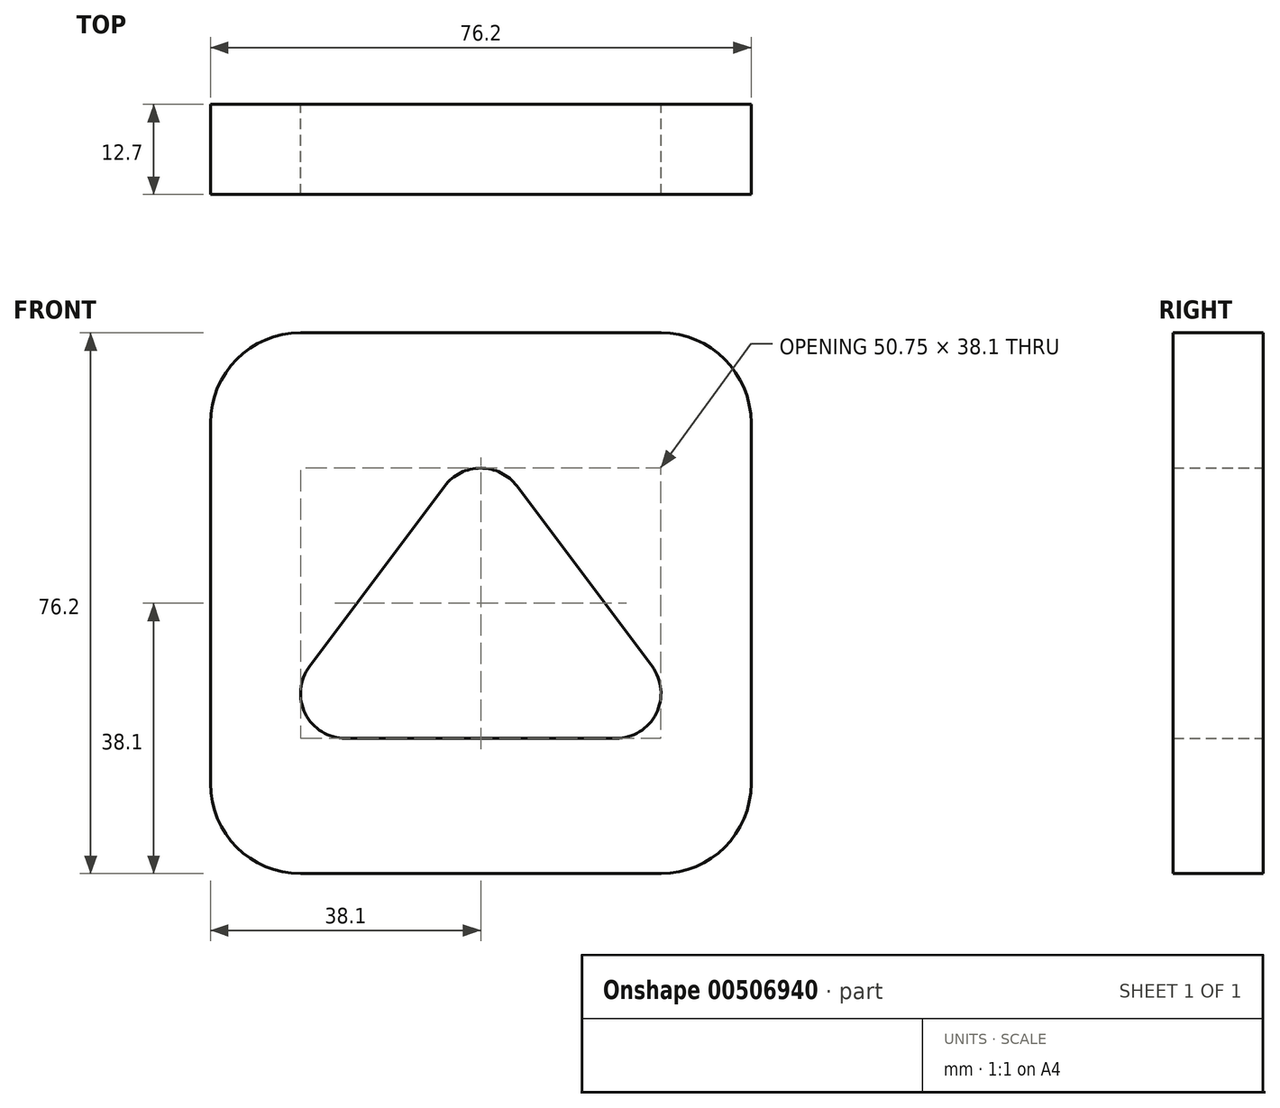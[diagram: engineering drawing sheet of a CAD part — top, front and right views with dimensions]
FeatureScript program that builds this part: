
annotation { "Feature Type Name" : "Feature", "Feature Type Description" : "" }
export const myFeature = defineFeature(function(context is Context, id is Id, definition is map)
    precondition{}
    {
        {
            var Q0;
            Q0=qCreatedBy(makeId("Front.planeOp"),FACE);
            var sketch = newSketch(context, id + "F0", { "sketchPlane" : qUnion([Q0])});
            skLineSegment(sketch, "E0", {"start": v(12.7, 0) * mm, "end": v(63.5, 0) * mm});
            skLineSegment(sketch, "E1", {"start": v(76.2, 12.7) * mm, "end": v(76.2, 63.5) * mm});
            skLineSegment(sketch, "E2", {"start": v(63.5, 76.2) * mm, "end": v(12.7, 76.2) * mm});
            skLineSegment(sketch, "E3", {"start": v(0, 63.5) * mm, "end": v(0, 12.7) * mm});
            skArc(sketch, "E4", {"start": v(13.97, 29.21) * mm, "mid": v(13.37, 22.56) * mm, "end": v(19.05, 19.05) * mm});
            skArc(sketch, "E5", {"start": v(57.15, 19.05) * mm, "mid": v(62.83, 22.56) * mm, "end": v(62.23, 29.21) * mm});
            skArc(sketch, "E6", {"start": v(43.18, 54.6) * mm, "mid": v(38.1, 57.15) * mm, "end": v(33.02, 54.6) * mm});
            skLineSegment(sketch, "E7", {"start": v(33.02, 54.6) * mm, "end": v(13.97, 29.21) * mm});
            skLineSegment(sketch, "E8", {"start": v(19.05, 19.05) * mm, "end": v(57.15, 19.05) * mm});
            skLineSegment(sketch, "E9", {"start": v(43.18, 54.6) * mm, "end": v(62.23, 29.21) * mm});
            skArc(sketch, "E10", {"start": v(12.7, 76.2) * mm, "mid": v(3.72, 72.48) * mm, "end": v(0, 63.5) * mm});
            skArc(sketch, "E11", {"start": v(76.2, 63.5) * mm, "mid": v(72.48, 72.48) * mm, "end": v(63.5, 76.2) * mm});
            skArc(sketch, "E12", {"start": v(0, 12.7) * mm, "mid": v(3.72, 3.72) * mm, "end": v(12.7, 0) * mm});
            skArc(sketch, "E13", {"start": v(63.5, 0) * mm, "mid": v(72.48, 3.72) * mm, "end": v(76.2, 12.7) * mm});
            skSolve(sketch);
        }
        {
            var Q0;
            Q0=makeQuery(id+"F0.imprint","IMPRINT",FACE,{"disambiguationData":[TD([[makeQuery(id+"F0.imprint","IMPRINT",EDGE,{"derivedFrom":sQuery(id+"F0.wireOp",EDGE,"E0")}),1.0]])]});
            extrude(context, id + "F1", {"entities" : qUnion([Q0]), "depth" : 12.7 * mm});
        }
    });
